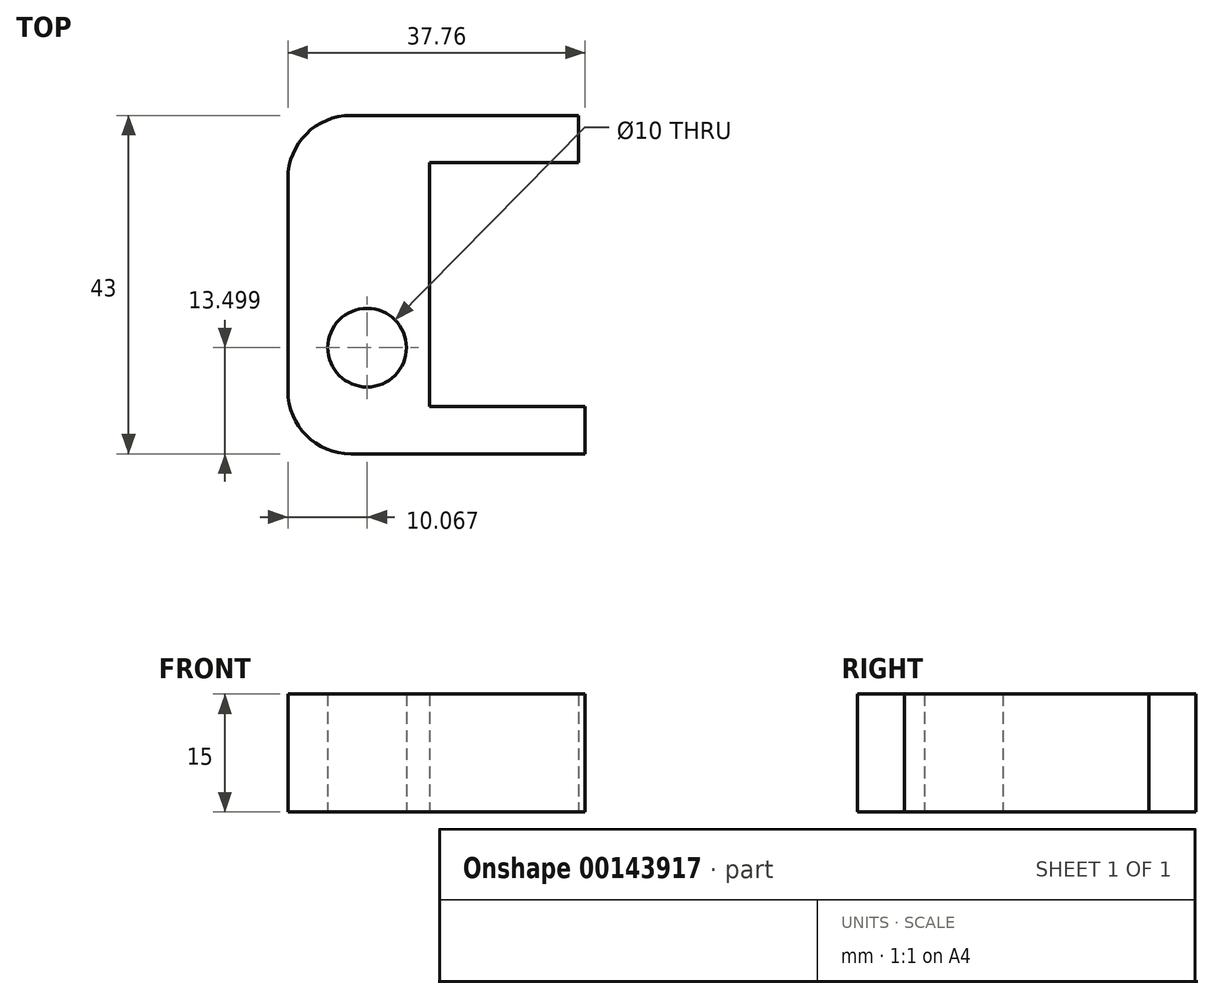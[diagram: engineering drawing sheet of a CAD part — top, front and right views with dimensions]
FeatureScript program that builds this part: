
annotation { "Feature Type Name" : "Feature", "Feature Type Description" : "" }
export const myFeature = defineFeature(function(context is Context, id is Id, definition is map)
    precondition{}
    {
        {
            var Q0;
            Q0=qCreatedBy(makeId("Top.planeOp"),FACE);
            var sketch = newSketch(context, id + "F0", { "sketchPlane" : qUnion([Q0])});
            skLineSegment(sketch, "E0", {"start": v(24.93, 37) * mm, "end": v(24.93, 43) * mm});
            skLineSegment(sketch, "E1", {"start": v(24.93, 43) * mm, "end": v(0, 43) * mm});
            skLineSegment(sketch, "E2", {"start": v(0, 43) * mm, "end": v(0, 0) * mm});
            skLineSegment(sketch, "E3", {"start": v(0, 0) * mm, "end": v(25.76, 0) * mm});
            skLineSegment(sketch, "E4", {"start": v(25.76, 0) * mm, "end": v(25.76, 6) * mm});
            skLineSegment(sketch, "E5", {"start": v(25.76, 6) * mm, "end": v(6, 6) * mm});
            skLineSegment(sketch, "E6", {"start": v(6, 6) * mm, "end": v(6, 37) * mm});
            skLineSegment(sketch, "E7", {"start": v(6, 37) * mm, "end": v(24.93, 37) * mm});
            skLineSegment(sketch, "E8.bottom", {"start": v(0, 43) * mm, "end": v(-4, 43) * mm});
            skLineSegment(sketch, "E8.top", {"start": v(0, 0) * mm, "end": v(-4, 0) * mm});
            skLineSegment(sketch, "E8.right", {"start": v(-12, 35) * mm, "end": v(-12, 8) * mm});
            skCircle(sketch, "E9", {"center": v(-1.93, 13.5) * mm, "radius": 5 * mm});
            skPoint(sketch, "E10.visualSharp", {"position": v(-12, 43) * mm});
            skArc(sketch, "E10.filletArc", {"start": v(-4, 43) * mm, "mid": v(-9.66, 40.66) * mm, "end": v(-12, 35) * mm});
            skPoint(sketch, "E11.visualSharp", {"position": v(-12, 0) * mm});
            skArc(sketch, "E11.filletArc", {"start": v(-12, 8) * mm, "mid": v(-9.66, 2.34) * mm, "end": v(-4, 0) * mm});
            skSolve(sketch);
        }
        {
            var Q0;
            {var subQ4=sQuery(id+"F0.wireOp",EDGE,"E8.bottom");Q0=makeQuery(id+"F0.imprint","IMPRINT",FACE,{"disambiguationData":[TD([[makeQuery(id+"F0.imprint","IMPRINT",EDGE,{"derivedFrom":subQ4}),1.0]])]});}
            var Q1;
            Q1=makeQuery(id+"F0.imprint","IMPRINT",FACE,{"disambiguationData":[TD([[makeQuery(id+"F0.imprint","IMPRINT",EDGE,{"derivedFrom":sQuery(id+"F0.wireOp",EDGE,"E0")}),1.0]])]});
            extrude(context, id + "F1", {"entities" : qUnion([Q0, Q1]), "depth" : 15 * mm});
        }
    });
